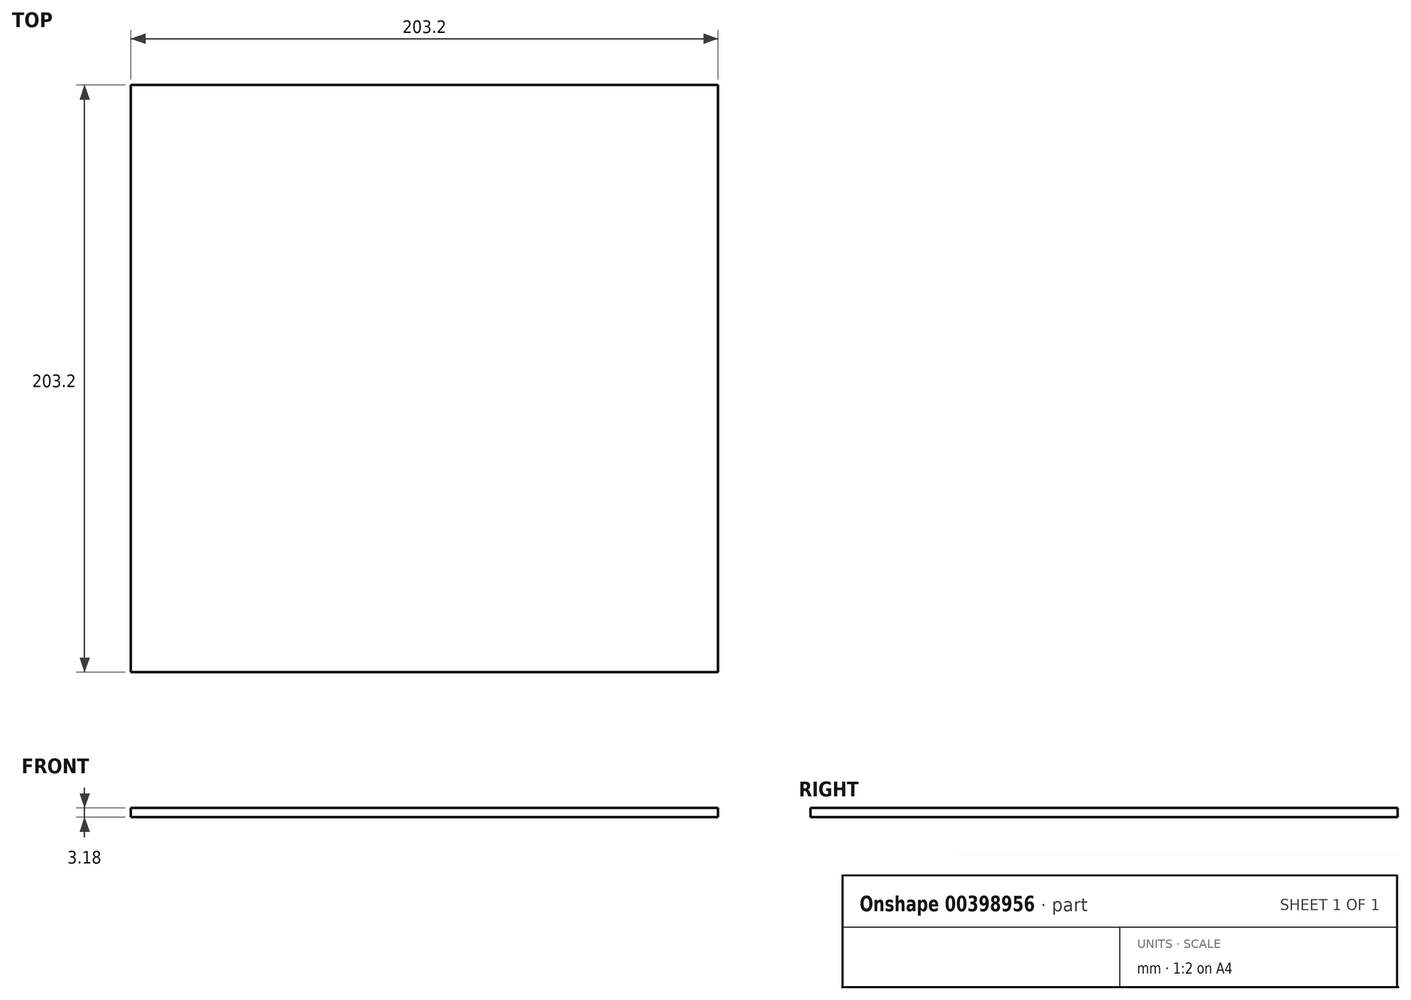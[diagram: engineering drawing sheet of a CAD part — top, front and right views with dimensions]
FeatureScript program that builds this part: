
annotation { "Feature Type Name" : "Feature", "Feature Type Description" : "" }
export const myFeature = defineFeature(function(context is Context, id is Id, definition is map)
    precondition{}
    {
        {
            var Q0;
            Q0=qCreatedBy(makeId("Top.planeOp"),FACE);
            var sketch = newSketch(context, id + "F0", { "sketchPlane" : qUnion([Q0])});
            skLineSegment(sketch, "E0.bottom", {"start": v(101.6, 101.6) * mm, "end": v(-101.6, 101.6) * mm});
            skLineSegment(sketch, "E0.top", {"start": v(101.6, -101.6) * mm, "end": v(-101.6, -101.6) * mm});
            skLineSegment(sketch, "E0.left", {"start": v(101.6, 101.6) * mm, "end": v(101.6, -101.6) * mm});
            skLineSegment(sketch, "E0.right", {"start": v(-101.6, 101.6) * mm, "end": v(-101.6, -101.6) * mm});
            skPoint(sketch, "E0.middle", {"position": v(0, 0) * mm});
            skSolve(sketch);
        }
        {
            var Q0;
            Q0 = qSketchRegion(id + "F0", true);
            extrude(context, id + "F1", {"entities" : qUnion([Q0]), "depth" : 3.17 * mm, "symmetric" : true});
        }
    });
